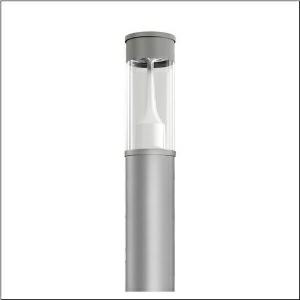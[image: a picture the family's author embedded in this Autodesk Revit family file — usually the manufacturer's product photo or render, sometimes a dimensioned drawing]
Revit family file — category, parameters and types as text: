
# Revit family: city-light_400_iq___p1_0a_5xa5305ff14hp_6c14
name_source: partatom
category: Lighting Fixtures
units: mm (PartAtom-declared; Revit-internal decimal feet)

## family parameters
Cut with Voids When Loaded = No
Host = Face
Light Source = No
Part Type = Normal
Room Calculation Point = No
Round Connector Dimension = Use Diameter
Shared = No

## types (1)
- --- (1 x LED, 4700 lm, 33.6 W, 3000K)
    Apparent Load = 34 VA
    CIE Flux Codes = 31 62 91 95 100
    Color Rendering = 70
    Color Temperature = 3000K
    Default Elevation = 1800 mm
    Description = City-Light 400 iQ, light pillar, Module 540 iQ-SR, primary light control with 3 zone facetted reflector, of plastic, silver coated, highly specular, structured, primary optical cover: cover, of PMMA, transparent, partly coated, light distribution: P1.0a, primary light characteristic: strongly asymmetric, LED, High Power LED, rated luminous flux: 4.700lm, luminous efficacy: 140lm/W, light colour: 730, colour temperature: 3000K, control gear: iQ Street-Remote, control: pre-setting: logarithmic dimming characteristic, Street-Remote, Auto-Match, Temp-Guard, Lumen-Switch, Night-Set, Smart-Wire, Light-Fading, Desk-Remote (wireless, voltage-free reading and setting of iQ features in the workshop via application-optimized NFC function/RFID function), optimised constant luminous flux control (CLO 2.0), with terminal, 6-pole, max. 2.5mm², mains connection: 230..240V, AC, 50/60Hz, start of lifetime: 34W, end of service life: 36W, reduction: 15W, luminaire housing, cylindrical, of extruded aluminium section, coated, Siteco® metallic grey (DB 702S), length: 4.694mm, diameter: 200mm, Module 540 iQ-SR, traffic white (RAL 9016), equipment: Power, protection rating (complete): IP65, insulation class (complete): insulation class II (safety insulation), certification: CE, ENEC, VDE, packaging unit: 1 piece

Light Distribution: P1.0a
    Height = 500 mm
    Lamp = 1 x LED
    Lamp Light Flux = 4700 lm
    Lamp Power = 33.6 W
    Lamp count = 1
    Length = 200 mm  [stored 0.656168 ft]
    Luminous efficacy = 140 lm/W
    Manufacturer = Siteco
    ModVariant = No
    Model = 5XA5305FF14HP
    Mounting Place = Floor
    Mounting Type = Freestanding
    Number of Poles = 1
    OnlyDefault = Yes
    Power Factor = 1
    Product Name = City-Light 400 iQ | P1.0a
    Product group = light pillar
    ProductGroupID = 1301
    Protection Class = Protection class II
    Protection Degree = IP 65
    RLX_Detail_Level = 1
    RLX_Emergency_Light_Flux = 0 lm
    RLX_Emergency_Type = 0
    RLX_Emergency_Type_DB = No
    RlxData = <blob elided: 53525 chars, md5=f5121644>
    Socket = socket
    Standby Power = 0 W
    System Light Flux = 4700 lm
    System Power = 34 W
    Type Comments = factory setting: luminous flux: 100 % | dim-lin: 254 | 695 mA
    Type Image = l_1006916.jpg
    URL = http://relux.com
    VarID = @adj_192746
    Voltage = 0 V
    Weight = 0.00 kg
    Width = 0 mm  [stored 0 ft]

note: [stored X ft] marks values corroborated as IEEE doubles in the binary element streams (Revit-internal decimal feet)

## geometry (parser evidence)
native form markers: Blend x4, Sweep x10
no freeform markers — native parametric forms only
